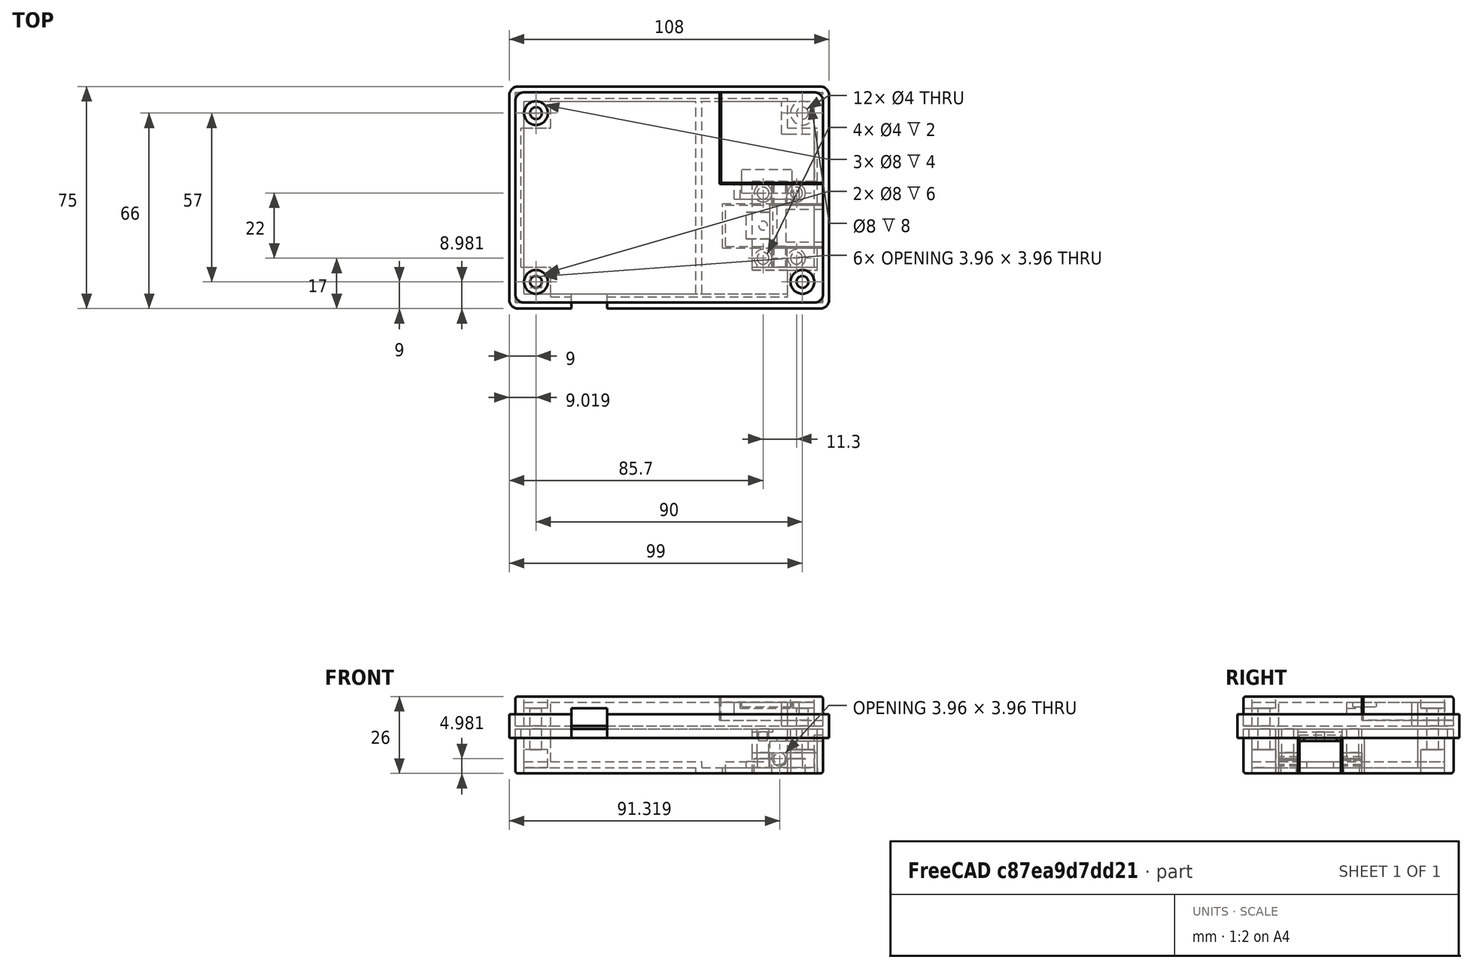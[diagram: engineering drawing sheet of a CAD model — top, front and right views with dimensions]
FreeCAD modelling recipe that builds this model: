
FCSTD DOCUMENT  (FreeCAD 0.14R3700 (Git))
Label: Arsenic_Detector_Enclosure
License: CC-BY 3.0
LicenseURL: http://creativecommons.org/licenses/by/3.0/
objects: Part::Box×76, Part::Cut×56, Part::Cylinder×36, Part::MultiFuse×13, Part::Fillet×7
note: 188 computed .brp shape members not serialized (recipe doc carries the construction recipe); baked Part::Feature solids carry a one-line shape summary decoded from their .brp

FEATURE [Part::Box] Box  label="Cube"
  Height = 15
  Length = 104
  Placement = pos=(-1,-1,0) rot=(0,0,1;0rad)
  Width = 71
FEATURE [Part::Box] Box001  label="Cube001"
  Height = 13
  Length = 100
  Placement = pos=(1,1,2) rot=(0,0,1;0rad)
  Width = 67
FEATURE [Part::Box] Box002  label="Cube002"
  Height = 13
  Length = 10
  Placement = pos=(1,1,2) rot=(0,0,1;0rad)
  Width = 10
FEATURE [Part::Box] Box003  label="Cube003"
  Height = 13
  Length = 10
  Placement = pos=(91,1,2) rot=(0,0,1;0rad)
  Width = 10
FEATURE [Part::Box] Box004  label="Cube004"
  Height = 13
  Length = 10
  Placement = pos=(1,58,2) rot=(0,0,1;0rad)
  Width = 10
FEATURE [Part::Box] Box005  label="Cube005"
  Height = 13
  Length = 10
  Placement = pos=(91,58,2) rot=(0,0,1;0rad)
  Width = 10
FEATURE [Part::Cylinder] Cylinder
  Angle = 360
  Height = 15
  Placement = pos=(6,6,0) rot=(0,0,1;0rad)
  Radius = 2
FEATURE [Part::Cylinder] Cylinder001
  Angle = 360
  Height = 15
  Placement = pos=(96,6,0) rot=(0,0,1;0rad)
  Radius = 2
FEATURE [Part::Cylinder] Cylinder002
  Angle = 360
  Height = 15
  Placement = pos=(6,63,0) rot=(0,0,1;0rad)
  Radius = 2
FEATURE [Part::Cylinder] Cylinder003
  Angle = 360
  Height = 15
  Placement = pos=(96,63,0) rot=(0,0,1;0rad)
  Radius = 2
FEATURE [Part::Cylinder] Cylinder004
  Angle = 360
  Height = 8
  Placement = pos=(6,6,0) rot=(0,0,1;0rad)
  Radius = 4
FEATURE [Part::Cylinder] Cylinder005
  Angle = 360
  Height = 8
  Placement = pos=(96,6,0) rot=(0,0,1;0rad)
  Radius = 4
FEATURE [Part::Cylinder] Cylinder006
  Angle = 360
  Height = 8
  Placement = pos=(96,63,0) rot=(0,0,1;0rad)
  Radius = 4
FEATURE [Part::Cylinder] Cylinder007
  Angle = 360
  Height = 8
  Placement = pos=(6,63,0) rot=(0,0,1;0rad)
  Radius = 4
FEATURE [Part::Box] Box006  label="Cube006"
  Height = 3
  Length = 12
  Placement = pos=(18,-1,12) rot=(0,0,1;0rad)
  Width = 2
FEATURE [Part::Box] Box007  label="Cube007"
  Height = 15
  Length = 24
  Placement = pos=(79,17.5,0) rot=(0,0,1;0rad)
  Width = 15
FEATURE [Part::Box] Box008  label="Cube008"
  Height = 10
  Length = 80
  Placement = pos=(11,1,2) rot=(0,0,1;0rad)
  Width = 1
FEATURE [Part::Box] Box009  label="Cube009"
  Height = 10
  Length = 80
  Placement = pos=(11,67,2) rot=(0,0,1;0rad)
  Width = 1
FEATURE [Part::Box] Box010  label="Cube010"
  Height = 10
  Length = 1
  Placement = pos=(100,39,2) rot=(0,0,1;0rad)
  Width = 19
FEATURE [Part::Box] Box011  label="Cube011"
  Height = 10
  Length = 1
  Placement = pos=(1,11,2) rot=(0,0,1;0rad)
  Width = 47
FEATURE [Part::Box] Box012  label="Cube012"
  Height = 8
  Length = 8
  Placement = pos=(92,6,0) rot=(0,0,1;0rad)
  Width = 10
FEATURE [Part::Box] Box016  label="Cube016"
  Height = 2
  Length = 57
  Placement = pos=(3,-1,0) rot=(0,0,1;0rad)
  Width = 3
FEATURE [Part::Box] Box017  label="Cube017"
  Height = 2
  Length = 57
  Placement = pos=(3,67,0) rot=(0,0,1;0rad)
  Width = 3
FEATURE [Part::Box] Box018  label="Cube018"
  Height = 2
  Length = 3
  Placement = pos=(-1,3,0) rot=(0,0,1;0rad)
  Width = 63
FEATURE [Part::Box] Box022  label="Cube022"
  Height = 2
  Length = 4
  Placement = pos=(-1,-1,0) rot=(0,0,1;0rad)
  Width = 4
FEATURE [Part::Box] Box023  label="Cube023"
  Height = 2
  Length = 4
  Placement = pos=(-1,66,0) rot=(0,0,1;0rad)
  Width = 4
FEATURE [Part::Box] Box025  label="Cube025"
  Height = 2
  Length = 2
  Placement = pos=(2,2,0) rot=(0,0,1;0rad)
  Width = 2
FEATURE [Part::Box] Box027  label="Cube027"
  Height = 2
  Length = 2
  Placement = pos=(2,65,0) rot=(0,0,1;0rad)
  Width = 2
FEATURE [Part::Box] Box029  label="Cube029"
  Height = 10
  Length = 104
  Placement = pos=(-1,-1,16) rot=(0,0,1;0rad)
  Width = 71
FEATURE [Part::Box] Box031  label="Cube031"
  Height = 8
  Length = 100
  Placement = pos=(1,1,16) rot=(0,0,1;0rad)
  Width = 67
FEATURE [Part::Cylinder] Cylinder016
  Angle = 360
  Height = 2
  Placement = pos=(96,63,16) rot=(0,0,1;0rad)
  Radius = 2
FEATURE [Part::Cylinder] Cylinder017
  Angle = 360
  Height = 10
  Placement = pos=(6,63,16) rot=(0,0,1;0rad)
  Radius = 2
FEATURE [Part::Cylinder] Cylinder018
  Angle = 360
  Height = 10
  Placement = pos=(96,6,16) rot=(0,0,1;0rad)
  Radius = 2
FEATURE [Part::Cylinder] Cylinder019
  Angle = 360
  Height = 10
  Placement = pos=(6,6,16) rot=(0,0,1;0rad)
  Radius = 2
FEATURE [Part::Cylinder] Cylinder020
  Angle = 360
  Height = 4
  Placement = pos=(6,6,22) rot=(0,0,1;0rad)
  Radius = 4
FEATURE [Part::Cylinder] Cylinder021
  Angle = 360
  Height = 4
  Placement = pos=(6,63,22) rot=(0,0,1;0rad)
  Radius = 4
FEATURE [Part::Cylinder] Cylinder023
  Angle = 360
  Height = 4
  Placement = pos=(96,6,22) rot=(0,0,1;0rad)
  Radius = 4
FEATURE [Part::Box] Box032  label="Cube032"
  Height = 8
  Length = 10
  Placement = pos=(1,1,16) rot=(0,0,1;0rad)
  Width = 10
FEATURE [Part::Box] Box033  label="Cube033"
  Height = 8
  Length = 10
  Placement = pos=(91,58,16) rot=(0,0,1;0rad)
  Width = 10
FEATURE [Part::Box] Box034  label="Cube034"
  Height = 8
  Length = 10
  Placement = pos=(91,1,16) rot=(0,0,1;0rad)
  Width = 10
FEATURE [Part::Box] Box035  label="Cube035"
  Height = 8
  Length = 10
  Placement = pos=(1,58,16) rot=(0,0,1;0rad)
  Width = 10
FEATURE [Part::Box] Box036  label="Cube036"
  Height = 6
  Length = 12
  Placement = pos=(18,-1,16) rot=(0,0,1;0rad)
  Width = 3
FEATURE [Part::Box] Box042  label="Cube042"
  Height = 8
  Length = 35
  Placement = pos=(68,39,18) rot=(0,0,1;0rad)
  Width = 31
FEATURE [Part::Box] Box073  label="Cube073"
  Height = 2
  Length = 22
  Placement = pos=(73,34,20) rot=(0,0,1;0rad)
  Width = 5
FEATURE [Part::Box] Box074  label="Cube074"
  Height = 2
  Length = 2
  Placement = pos=(73,34,22) rot=(0,0,1;0rad)
  Width = 5
FEATURE [Part::Box] Box075  label="Cube075"
  Height = 2
  Length = 2
  Placement = pos=(93,34,22) rot=(0,0,1;0rad)
  Width = 5
FEATURE [Part::Box] Box076  label="Cube076"
  Height = 8
  Length = 34.5
  Placement = pos=(68.5,39.5,18) rot=(0,0,1;0rad)
  Width = 30.5
FEATURE [Part::Box] Box077  label="Cube077"
  Height = 6
  Length = 31.5
  Placement = pos=(68.5,39.5,18) rot=(0,0,1;0rad)
  Width = 27.5
FEATURE [Part::Box] Box078  label="Cube078"
  Height = 1.5
  Length = 17
  Placement = pos=(75.5,36,22.5) rot=(0,0,1;0rad)
  Width = 8
FEATURE [Part::Box] Box079  label="Cube079"
  Height = 8
  Length = 2
  Placement = pos=(89,56,16) rot=(0,0,1;0rad)
  Width = 11
FEATURE [Part::Box] Box080  label="Cube080"
  Height = 8
  Length = 9
  Placement = pos=(91,56,16) rot=(0,0,1;0rad)
  Width = 2
FEATURE [Part::Cut] Cut057
  Base = -> Box076
  Tool = -> Box077
FEATURE [Part::MultiFuse] Fusion017
  Shapes = -> [Cut057,Box078,Box080,Box079]
FEATURE [Part::Fillet] Fillet016
  Base = -> Fusion017
  Edges = 1 edges r=3: [Edge3]
FEATURE [Part::Cylinder] Cylinder024
  Angle = 360
  Height = 12
  Placement = pos=(2,2,11) rot=(0,0,1;0rad)
  Radius = 3
FEATURE [Part::Cylinder] Cylinder025
  Angle = 360
  Height = 12
  Placement = pos=(100,2,11) rot=(0,0,1;0rad)
  Radius = 3
FEATURE [Part::Cylinder] Cylinder026
  Angle = 360
  Height = 12
  Placement = pos=(2,67,11) rot=(0,0,1;0rad)
  Radius = 3
FEATURE [Part::Cylinder] Cylinder027
  Angle = 360
  Height = 12
  Placement = pos=(100,67,11) rot=(0,0,1;0rad)
  Radius = 3
FEATURE [Part::Box] Box081  label="Cube081"
  Height = 8
  Length = 98
  Placement = pos=(2,70,12) rot=(0,0,1;0rad)
  Width = 2
FEATURE [Part::Box] Box082  label="Cube082"
  Height = 8
  Length = 5
  Placement = pos=(100,67,12) rot=(0,0,1;0rad)
  Width = 5
FEATURE [Part::Box] Box083  label="Cube083"
  Height = 8
  Length = 5
  Placement = pos=(100,-3,12) rot=(0,0,1;0rad)
  Width = 5
FEATURE [Part::Box] Box084  label="Cube084"
  Height = 8
  Length = 70
  Placement = pos=(30,-3,12) rot=(0,0,1;0rad)
  Width = 2
FEATURE [Part::Box] Box085  label="Cube085"
  Height = 8
  Length = 5
  Placement = pos=(-3,-3,12) rot=(0,0,1;0rad)
  Width = 5
FEATURE [Part::Box] Box086  label="Cube086"
  Height = 8
  Length = 5
  Placement = pos=(-3,67,12) rot=(0,0,1;0rad)
  Width = 5
FEATURE [Part::Box] Box087  label="Cube087"
  Height = 8
  Length = 2
  Placement = pos=(103,2,12) rot=(0,0,1;0rad)
  Width = 65
FEATURE [Part::Box] Box088  label="Cube088"
  Height = 8
  Length = 2
  Placement = pos=(-3,2,12) rot=(0,0,1;0rad)
  Width = 65
FEATURE [Part::Box] Box089  label="Cube089"
  Height = 8
  Length = 16
  Placement = pos=(2,-3,12) rot=(0,0,1;0rad)
  Width = 2
FEATURE [Part::MultiFuse] Fusion018
  Shapes = -> [Box081,Box082,Box083,Box084,Box085,Box086,Box087,Box089,Box088]
FEATURE [Part::Cut] Cut058
  Base = -> Fusion018
  Tool = -> Cylinder027
FEATURE [Part::Cut] Cut059
  Base = -> Cut058
  Tool = -> Cylinder026
FEATURE [Part::Cut] Cut060
  Base = -> Cut059
  Tool = -> Cylinder025
FEATURE [Part::Cut] Cut061
  Base = -> Cut060
  Tool = -> Cylinder024
FEATURE [Part::Fillet] Fillet018
  Base = -> Cut061
  Edges = 4 edges r=3: [Edge3,Edge25,Edge46,Edge74]
FEATURE [Part::Fillet] Fillet017
  Base = -> Fillet016
  Edges = 3 edges r=1: [Edge1,Edge5,Edge6]
FEATURE [Part::Box] Box040  label="Cube040"
  Height = 8
  Length = 1
  Placement = pos=(1,11,16) rot=(0,0,1;0rad)
  Width = 47
FEATURE [Part::Box] Box038  label="Cube038"
  Height = 8
  Length = 80
  Placement = pos=(11,67,16) rot=(0,0,1;0rad)
  Width = 1
FEATURE [Part::Box] Box039  label="Cube039"
  Height = 8
  Length = 1
  Placement = pos=(100,11,16) rot=(0,0,1;0rad)
  Width = 47
FEATURE [Part::Box] Box037  label="Cube037"
  Height = 8
  Length = 80
  Placement = pos=(11,1,16) rot=(0,0,1;0rad)
  Width = 1
FEATURE [Part::MultiFuse] Fusion022
  Shapes = -> [Box075,Box074,Box073]
FEATURE [Part::Cut] Cut073
  Base = -> Box029
  Tool = -> Box031
FEATURE [Part::MultiFuse] Fusion023
  Shapes = -> [Cut073,Box037,Box039,Box032,Box035,Box034,Box033,Box040,Box038]
FEATURE [Part::Cut] Cut074
  Base = -> Fusion023
  Tool = -> Box042
FEATURE [Part::Cut] Cut075
  Base = -> Cut074
  Tool = -> Box036
FEATURE [Part::Cut] Cut076
  Base = -> Cut075
  Tool = -> Cylinder016
FEATURE [Part::Cut] Cut077
  Base = -> Cut076
  Tool = -> Cylinder023
FEATURE [Part::Cut] Cut078
  Base = -> Cut077
  Tool = -> Cylinder021
FEATURE [Part::Cut] Cut079
  Base = -> Cut078
  Tool = -> Cylinder020
FEATURE [Part::Cut] Cut080
  Base = -> Cut079
  Tool = -> Cylinder019
FEATURE [Part::Cut] Cut081
  Base = -> Cut080
  Tool = -> Cylinder017
FEATURE [Part::Cut] Cut082
  Base = -> Cut081
  Tool = -> Cylinder018
FEATURE [Part::Fillet] Fillet019
  Base = -> Cut082
  Edges = 4 edges r=3: [Edge1,Edge3,Edge10,Edge19]
FEATURE [Part::Fillet] Fillet020
  Base = -> Fillet019
  Edges = 7 edges r=1: [Edge1,Edge5,Edge6,Edge9,Edge10,Edge11,Edge12]
FEATURE [Part::Box] Box090  label="Cube090"
  Height = 2
  Length = 10
  Placement = pos=(69,17.5,0) rot=(0,0,1;0rad)
  Width = 15
FEATURE [Part::Box] Box091  label="Cube091"
  Height = 2
  Length = 61
  Placement = pos=(-1,-1,0) rot=(0,0,1;0rad)
  Width = 71
FEATURE [Part::Box] Box092  label="Cube092"
  Height = 2
  Length = 51
  Placement = pos=(11,2,2) rot=(0,0,1;0rad)
  Width = 65
FEATURE [Part::Box] Box093  label="Cube093"
  Height = 2
  Length = 9
  Placement = pos=(2,11,2) rot=(0,0,1;0rad)
  Width = 47
FEATURE [Part::Cylinder] Cylinder029
  Angle = 360
  Height = 15
  Placement = pos=(94,14,0) rot=(0,0,1;0rad)
  Radius = 2
FEATURE [Part::Cylinder] Cylinder030
  Angle = 360
  Height = 15
  Placement = pos=(94,36,0) rot=(0,0,1;0rad)
  Radius = 2
FEATURE [Part::Cylinder] Cylinder031
  Angle = 360
  Height = 15
  Placement = pos=(82.7,14,0) rot=(0,0,1;0rad)
  Radius = 2
FEATURE [Part::Cylinder] Cylinder032
  Angle = 360
  Height = 15
  Placement = pos=(82.7,36,0) rot=(0,0,1;0rad)
  Radius = 2
FEATURE [Part::Box] Box094  label="Cube094"
  Height = 8
  Length = 22
  Placement = pos=(79,11,7) rot=(0,0,1;0rad)
  Width = 6.5
FEATURE [Part::Box] Box095  label="Cube095"
  Height = 8
  Length = 22
  Placement = pos=(79,32.5,7) rot=(0,0,1;0rad)
  Width = 6.5
FEATURE [Part::Box] Box098  label="Cube098"
  Height = 1
  Length = 7
  Placement = pos=(79,17.5,14) rot=(0,0,1;0rad)
  Width = 15
FEATURE [Part::Cylinder] Cylinder033
  Angle = 360
  Height = 3
  Placement = pos=(82.7,25,11) rot=(0,0,1;0rad)
  Radius = 1.5
FEATURE [Part::Cylinder] Cylinder034
  Angle = 360
  Height = 15
  Placement = pos=(82.7,14,0) rot=(0,0,1;0rad)
  Radius = 2
FEATURE [Part::Box] Box099  label="Cube099"
  Height = 15
  Length = 22
  Placement = pos=(79,32,0) rot=(0,0,1;0rad)
  Width = 8
FEATURE [Part::Box] Box100  label="Cube100"
  Height = 15
  Length = 22
  Placement = pos=(79,10,0) rot=(0,0,1;0rad)
  Width = 8
FEATURE [Part::Box] Box101  label="Cube101"
  Height = 7
  Length = 22
  Placement = pos=(79,11,0) rot=(0,0,1;0rad)
  Width = 6.5
FEATURE [Part::Box] Box102  label="Cube102"
  Height = 7
  Length = 22
  Placement = pos=(79,32.5,0) rot=(0,0,1;0rad)
  Width = 6.5
FEATURE [Part::Cylinder] Cylinder037
  Angle = 360
  Height = 28
  Placement = pos=(88.3,39,5) rot=(1,0,0;1.5708rad)
  Radius = 2.5
FEATURE [Part::Box] Box103  label="Cube103"
  Height = 2.5
  Length = 5
  Placement = pos=(85.7,10.5,4.5) rot=(0,0,1;0rad)
  Width = 8
FEATURE [Part::Box] Box104  label="Cube104"
  Height = 2.5
  Length = 5
  Placement = pos=(85.7,31.5,4.5) rot=(0,0,1;0rad)
  Width = 8
FEATURE [Part::Cylinder] Cylinder039
  Angle = 360
  Height = 15
  Placement = pos=(94,14,0) rot=(0,0,1;0rad)
  Radius = 2
FEATURE [Part::Cylinder] Cylinder040
  Angle = 360
  Height = 15
  Placement = pos=(94,36,0) rot=(0,0,1;0rad)
  Radius = 2
FEATURE [Part::Cylinder] Cylinder041
  Angle = 360
  Height = 15
  Placement = pos=(94,14,-10) rot=(0,0,1;0rad)
  Radius = 3
FEATURE [Part::Box] Box105  label="Cube105"
  Height = 11
  Length = 23
  Placement = pos=(80,18,0) rot=(0,0,1;0rad)
  Width = 14
FEATURE [Part::Cylinder] Cylinder042
  Angle = 360
  Height = 28
  Placement = pos=(88.3,39,5) rot=(1,0,0;1.5708rad)
  Radius = 2
FEATURE [Part::Cylinder] Cylinder043
  Angle = 360
  Height = 30
  Placement = pos=(88.3,40,5) rot=(1,0,0;1.5708rad)
  Radius = 2.5
FEATURE [Part::Cylinder] Cylinder044
  Angle = 360
  Height = 30
  Placement = pos=(88.3,40,5) rot=(1,0,0;1.5708rad)
  Radius = 2.5
FEATURE [Part::Box] Box106  label="Cube106"
  Height = 9
  Length = 5
  Placement = pos=(80,18,2) rot=(0,0,1;0rad)
  Width = 14
FEATURE [Part::Box] Box107  label="Cube107"
  Height = 4
  Length = 10
  Placement = pos=(70,18,0) rot=(0,0,1;0rad)
  Width = 14
FEATURE [Part::Cylinder] Cylinder045
  Angle = 360
  Height = 15
  Placement = pos=(94,36,-10) rot=(0,0,1;0rad)
  Radius = 3
FEATURE [Part::Cylinder] Cylinder046
  Angle = 360
  Height = 15
  Placement = pos=(82.7,36,-10) rot=(0,0,1;0rad)
  Radius = 3
FEATURE [Part::Cylinder] Cylinder047
  Angle = 360
  Height = 15
  Placement = pos=(82.7,14,-10) rot=(0,0,1;0rad)
  Radius = 3
FEATURE [Part::Box] Box109  label="Cube109"
  Height = 5
  Length = 4
  Placement = pos=(80.7,10.5,0) rot=(0,0,1;0rad)
  Width = 3
FEATURE [Part::Box] Box110  label="Cube110"
  Height = 5
  Length = 4
  Placement = pos=(80.7,36.5,0) rot=(0,0,1;0rad)
  Width = 3
FEATURE [Part::Box] Box111  label="Cube111"
  Height = 5
  Length = 4
  Placement = pos=(92,10.5,0) rot=(0,0,1;0rad)
  Width = 3
FEATURE [Part::Box] Box112  label="Cube112"
  Height = 5
  Length = 4
  Placement = pos=(92,36.5,0) rot=(0,0,1;0rad)
  Width = 3
FEATURE [Part::Cut] Cut
  Base = -> Box
  Tool = -> Box001
FEATURE [Part::Cut] Cut120
  Base = -> Cut
  Tool = -> Box007
FEATURE [Part::Cut] Cut121
  Base = -> Cut120
  Tool = -> Box006
FEATURE [Part::MultiFuse] Fusion
  Shapes = -> [Box008,Box009,Box010,Box011,Cut121]
FEATURE [Part::MultiFuse] Fusion029
  Shapes = -> [Fusion,Box003,Box004,Box005,Box002]
FEATURE [Part::Cut] Cut122
  Base = -> Fusion029
  Tool = -> Box091
FEATURE [Part::Cut] Cut123
  Base = -> Cut122
  Tool = -> Cylinder001
FEATURE [Part::Cut] Cut124
  Base = -> Cut123
  Tool = -> Cylinder002
FEATURE [Part::Cut] Cut125
  Base = -> Cut124
  Tool = -> Cylinder003
FEATURE [Part::Cut] Cut126
  Base = -> Cut125
  Tool = -> Cylinder006
FEATURE [Part::Cut] Cut127
  Base = -> Cut126
  Tool = -> Cylinder007
FEATURE [Part::Cut] Cut128
  Base = -> Cut127
  Tool = -> Cylinder
FEATURE [Part::Cut] Cut129
  Base = -> Cut128
  Tool = -> Cylinder004
FEATURE [Part::Cut] Cut130
  Base = -> Cut129
  Tool = -> Cylinder005
FEATURE [Part::MultiFuse] Fusion030
  Shapes = -> [Box022,Box023,Box018,Box017,Box016]
FEATURE [Part::Cut] Cut131
  Base = -> Fusion030
  Tool = -> Box027
FEATURE [Part::Cut] Cut132
  Base = -> Cut131
  Tool = -> Box025
FEATURE [Part::MultiFuse] Fusion031
  Shapes = -> [Cut132,Cut130]
FEATURE [Part::MultiFuse] Fusion032
  Shapes = -> [Box093,Box092,Fusion031]
FEATURE [Part::Cut] Cut133
  Base = -> Fusion032
  Tool = -> Box090
FEATURE [Part::Cut] Cut134
  Base = -> Cut133
  Tool = -> Box100
FEATURE [Part::Cut] Cut135
  Base = -> Cut134
  Tool = -> Box099
FEATURE [Part::Cut] Cut136
  Base = -> Cut135
  Tool = -> Box012
FEATURE [Part::Fillet] Fillet
  Base = -> Cut136
  Edges = 11 edges r=1: [Edge1,Edge10,Edge11,Edge15,Edge16,Edge40,Edge51,Edge80,Edge100,Edge108,Edge110]
FEATURE [Part::MultiFuse] Fusion033
  Shapes = -> [Box098,Cylinder033,Box094,Box095]
FEATURE [Part::Cut] Cut145
  Base = -> Fusion033
  Tool = -> Cylinder029
FEATURE [Part::Cut] Cut146
  Base = -> Cut145
  Tool = -> Cylinder032
FEATURE [Part::Cut] Cut147
  Base = -> Cut146
  Tool = -> Cylinder030
FEATURE [Part::Cut] Cut148
  Base = -> Cut147
  Tool = -> Cylinder031
FEATURE [Part::Cylinder] Cylinder038
  Angle = 360
  Height = 15
  Placement = pos=(82.7,36,0) rot=(0,0,1;0rad)
  Radius = 2
FEATURE [Part::Cut] Cut149
  Base = -> Box102
  Tool = -> Box104
FEATURE [Part::Cut] Cut150
  Base = -> Cut149
  Tool = -> Cylinder043
FEATURE [Part::Cut] Cut151
  Base = -> Cut150
  Tool = -> Cylinder038
FEATURE [Part::Cut] Cut152
  Base = -> Cut151
  Tool = -> Cylinder040
FEATURE [Part::Cut] Cut153
  Base = -> Cut152
  Tool = -> Cylinder045
FEATURE [Part::Cut] Cut154
  Base = -> Cut153
  Tool = -> Cylinder046
FEATURE [Part::Cut] Cut155
  Base = -> Cut154
  Tool = -> Box110
FEATURE [Part::Cut] Cut156
  Base = -> Cut155
  Tool = -> Box112
FEATURE [Part::Cut] Cut157
  Base = -> Box101
  Tool = -> Box103
FEATURE [Part::Cut] Cut158
  Base = -> Cut157
  Tool = -> Cylinder037
FEATURE [Part::Cut] Cut159
  Base = -> Cut158
  Tool = -> Cylinder039
FEATURE [Part::Cut] Cut160
  Base = -> Cut159
  Tool = -> Cylinder034
FEATURE [Part::Cut] Cut161
  Base = -> Cut160
  Tool = -> Cylinder047
FEATURE [Part::Cut] Cut162
  Base = -> Cut161
  Tool = -> Cylinder041
FEATURE [Part::Cut] Cut163
  Base = -> Cut162
  Tool = -> Cylinder044
FEATURE [Part::Cut] Cut164
  Base = -> Cut163
  Tool = -> Box109
FEATURE [Part::Cut] Cut165
  Base = -> Cut164
  Tool = -> Box111
FEATURE [Part::MultiFuse] Fusion034
  Shapes = -> [Cylinder042,Box105,Box107]
FEATURE [Part::Cut] Cut166
  Base = -> Fusion034
  Tool = -> Box106
FEATURE [Part::Fillet] Fillet021
  Base = -> Cut166
  Edges = 1 edges r=1: [Edge13]
FEATURE [Part::Box] Box113  label="Cube113"
  Height = 2
  Length = 5
  Placement = pos=(80,28,2) rot=(0,0,1;0rad)
  Width = 4
FEATURE [Part::Box] Box114  label="Cube114"
  Height = 2
  Length = 5
  Placement = pos=(80,18,2) rot=(0,0,1;0rad)
  Width = 4
FEATURE [Part::MultiFuse] Fusion035
  Shapes = -> [Fillet021,Box113,Box114]
FEATURE [Part::Box] Box115  label="Cube115"
  Height = 1
  Length = 3
  Placement = pos=(87.5,19.5,11) rot=(0,0,1;0rad)
  Width = 11
FEATURE [Part::Box] Box116  label="Cube116"
  Height = 1
  Length = 15.5
  Placement = pos=(87.5,30.5,11) rot=(0,0,1;0rad)
  Width = 1.5
FEATURE [Part::Box] Box117  label="Cube117"
  Height = 1
  Length = 15.5
  Placement = pos=(87.5,18,11) rot=(0,0,1;0rad)
  Width = 1.5
FEATURE [Part::Box] Box118  label="Cube118"
  Height = 1
  Length = 3
  Placement = pos=(100,18,12) rot=(0,0,1;0rad)
  Width = 14
FEATURE [Part::MultiFuse] Fusion036
  Shapes = -> [Box115,Box116,Box117,Box118]
FEATURE [Part::Box] Box119  label="Cube119"
  Height = 4
  Length = 8
  Placement = pos=(77,20.5,2) rot=(0,0,1;0rad)
  Width = 9
FEATURE [Part::Cut] Cut167
  Base = -> Fusion035
  Tool = -> Box119
